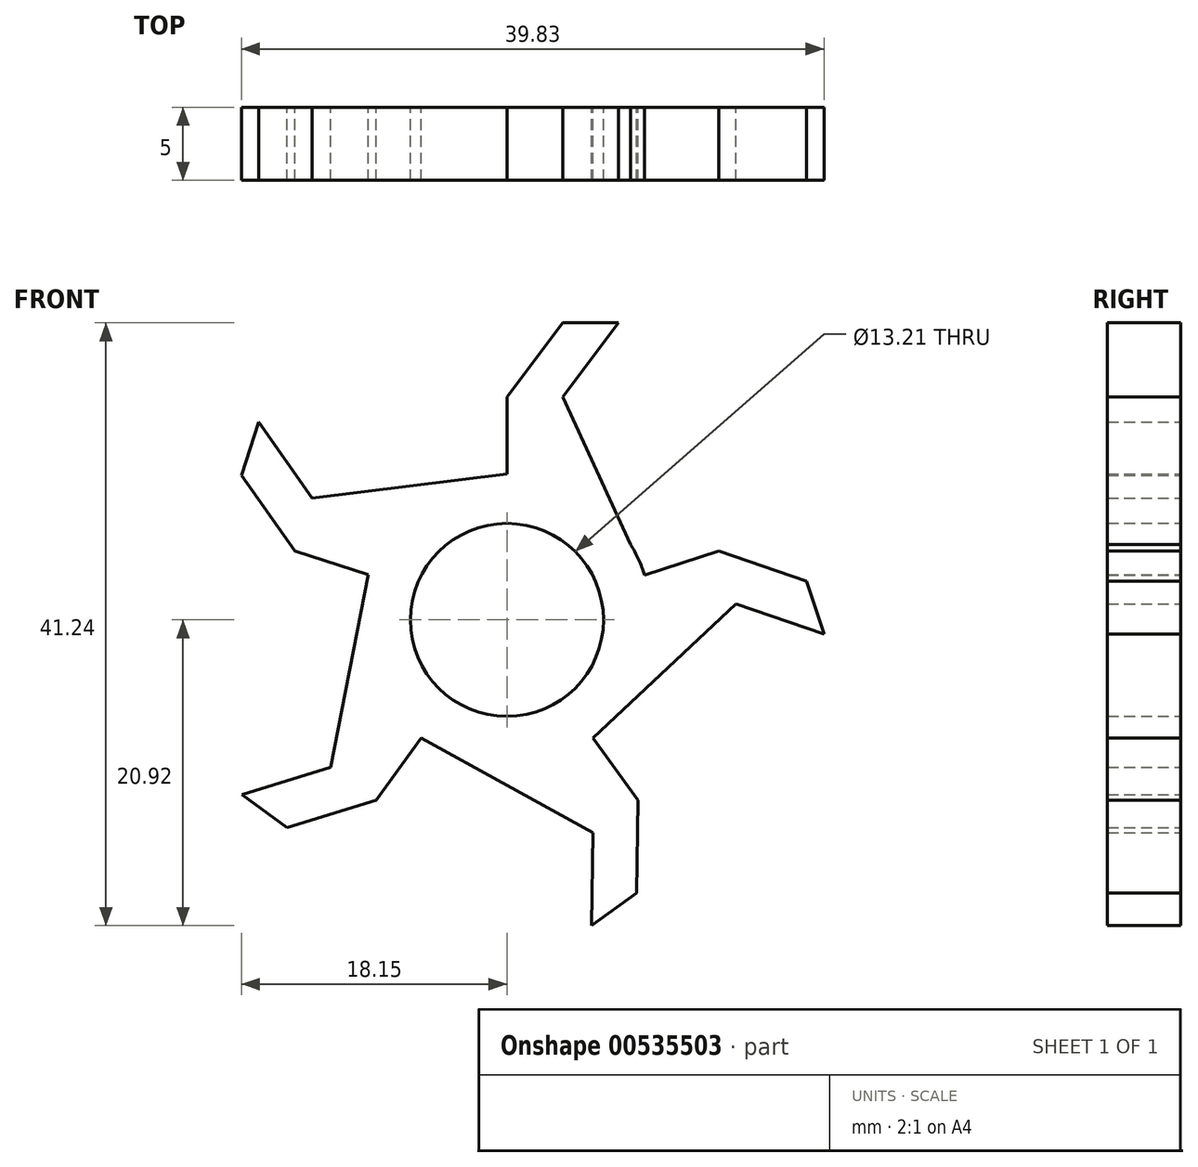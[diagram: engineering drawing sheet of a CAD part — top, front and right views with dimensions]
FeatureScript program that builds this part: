
annotation { "Feature Type Name" : "Feature", "Feature Type Description" : "" }
export const myFeature = defineFeature(function(context is Context, id is Id, definition is map)
    precondition{}
    {
        {
            var Q0;
            Q0=qCreatedBy(makeId("Front.planeOp"),FACE);
            var sketch = newSketch(context, id + "F0", { "sketchPlane" : qUnion([Q0])});
            skCircle(sketch, "E0", {"center": v(0, 0) * mm, "radius": 6.6 * mm});
            skCircle(sketch, "E1", {"center": v(0, 0) * mm, "radius": 9.9 * mm});
            skLineSegment(sketch, "E2", {"start": v(0, 0) * mm, "end": v(0, 15.24) * mm});
            skLineSegment(sketch, "E3", {"start": v(0, 0) * mm, "end": v(3.81, 0) * mm});
            skLineSegment(sketch, "E4", {"start": v(3.81, 0) * mm, "end": v(3.81, 15.24) * mm});
            skLineSegment(sketch, "E5", {"start": v(3.81, 15.24) * mm, "end": v(0, 15.24) * mm});
            skLineSegment(sketch, "E6", {"start": v(3.8, 15.24) * mm, "end": v(7.62, 20.32) * mm});
            skLineSegment(sketch, "E7", {"start": v(7.62, 20.32) * mm, "end": v(3.81, 20.32) * mm});
            skLineSegment(sketch, "E8", {"start": v(3.8, 20.32) * mm, "end": v(0, 15.24) * mm});
            skLineSegment(sketch, "E9", {"start": v(3.81, 15.24) * mm, "end": v(3.81, 20.32) * mm});
            skLineSegment(sketch, "E10.1.0", {"start": v(-16.97, 13.53) * mm, "end": v(-18.15, 9.9) * mm});
            skLineSegment(sketch, "E10.1.1", {"start": v(-18.15, 9.9) * mm, "end": v(-14.5, 4.7) * mm});
            skLineSegment(sketch, "E10.1.2", {"start": v(-13.32, 8.33) * mm, "end": v(-16.97, 13.53) * mm});
            skLineSegment(sketch, "E10.1.3", {"start": v(-13.32, 8.33) * mm, "end": v(-14.5, 4.7) * mm});
            skLineSegment(sketch, "E10.1.4", {"start": v(0, 0) * mm, "end": v(-14.5, 4.7) * mm});
            skLineSegment(sketch, "E10.1.5", {"start": v(1.18, 3.62) * mm, "end": v(-13.32, 8.33) * mm});
            skLineSegment(sketch, "E10.1.6", {"start": v(0, 0) * mm, "end": v(1.18, 3.62) * mm});
            skLineSegment(sketch, "E10.2.0", {"start": v(-18.1, -11.96) * mm, "end": v(-15.03, -14.2) * mm});
            skLineSegment(sketch, "E10.2.1", {"start": v(-15.03, -14.2) * mm, "end": v(-8.96, -12.33) * mm});
            skLineSegment(sketch, "E10.2.2", {"start": v(-12.04, -10.09) * mm, "end": v(-18.1, -11.96) * mm});
            skLineSegment(sketch, "E10.2.3", {"start": v(-12.04, -10.09) * mm, "end": v(-8.96, -12.33) * mm});
            skLineSegment(sketch, "E10.2.4", {"start": v(0, 0) * mm, "end": v(-8.96, -12.33) * mm});
            skLineSegment(sketch, "E10.2.5", {"start": v(-3.08, 2.24) * mm, "end": v(-12.04, -10.09) * mm});
            skLineSegment(sketch, "E10.2.6", {"start": v(0, 0) * mm, "end": v(-3.08, 2.24) * mm});
            skLineSegment(sketch, "E10.3.0", {"start": v(5.78, -20.92) * mm, "end": v(8.86, -18.68) * mm});
            skLineSegment(sketch, "E10.3.1", {"start": v(8.86, -18.68) * mm, "end": v(8.96, -12.33) * mm});
            skLineSegment(sketch, "E10.3.2", {"start": v(5.88, -14.57) * mm, "end": v(5.78, -20.92) * mm});
            skLineSegment(sketch, "E10.3.3", {"start": v(5.88, -14.57) * mm, "end": v(8.96, -12.33) * mm});
            skLineSegment(sketch, "E10.3.4", {"start": v(0, 0) * mm, "end": v(8.96, -12.33) * mm});
            skLineSegment(sketch, "E10.3.5", {"start": v(-3.08, -2.24) * mm, "end": v(5.88, -14.57) * mm});
            skLineSegment(sketch, "E10.3.6", {"start": v(0, 0) * mm, "end": v(-3.08, -2.24) * mm});
            skLineSegment(sketch, "E10.4.0", {"start": v(21.68, -0.97) * mm, "end": v(20.5, 2.66) * mm});
            skLineSegment(sketch, "E10.4.1", {"start": v(20.5, 2.66) * mm, "end": v(14.5, 4.7) * mm});
            skLineSegment(sketch, "E10.4.2", {"start": v(15.67, 1.09) * mm, "end": v(21.68, -0.97) * mm});
            skLineSegment(sketch, "E10.4.3", {"start": v(15.67, 1.09) * mm, "end": v(14.5, 4.7) * mm});
            skLineSegment(sketch, "E10.4.4", {"start": v(0, 0) * mm, "end": v(14.5, 4.7) * mm});
            skLineSegment(sketch, "E10.4.5", {"start": v(1.18, -3.62) * mm, "end": v(15.67, 1.09) * mm});
            skLineSegment(sketch, "E10.4.6", {"start": v(0, 0) * mm, "end": v(1.18, -3.62) * mm});
            skLineSegment(sketch, "E11", {"start": v(-13.32, 8.33) * mm, "end": v(0, 9.98) * mm});
            skLineSegment(sketch, "E12", {"start": v(-12.04, -10.09) * mm, "end": v(-9.5, 3.08) * mm});
            skLineSegment(sketch, "E13", {"start": v(5.88, -14.57) * mm, "end": v(-5.87, -8.08) * mm});
            skLineSegment(sketch, "E14", {"start": v(15.67, 1.09) * mm, "end": v(5.87, -8.08) * mm});
            skLineSegment(sketch, "E15", {"start": v(3.8, 15.24) * mm, "end": v(9.42, 3.06) * mm});
            skSolve(sketch);
        }
        {
            var Q0;
            Q0 = qSketchRegion(id + "F0", true);
            var Q1;
            {var subQ0=sQuery(id+"F0.wireOp",EDGE,"E10.2.5");var subQ1=sQuery(id+"F0.wireOp",EDGE,"E0");var subQ2=makeQuery(id+"F0.imprint","INTERSECT",VERTEX,{"derivedFrom":[subQ1,subQ0]});Q1=makeQuery(id+"F0.imprint","IMPRINT",FACE,{"disambiguationData":[TD([[makeQuery(id+"F0.imprint","IMPRINT",EDGE,{"disambiguationData":[TD([[subQ2,-1.0]])],"derivedFrom":subQ1}),-1.0]])]});}
            var Q2;
            {var subQ0=sQuery(id+"F0.wireOp",EDGE,"E10.3.5");var subQ1=sQuery(id+"F0.wireOp",EDGE,"E0");var subQ2=makeQuery(id+"F0.imprint","INTERSECT",VERTEX,{"derivedFrom":[subQ1,subQ0]});Q2=makeQuery(id+"F0.imprint","IMPRINT",FACE,{"disambiguationData":[TD([[makeQuery(id+"F0.imprint","IMPRINT",EDGE,{"disambiguationData":[TD([[subQ2,-1.0]])],"derivedFrom":subQ1}),-1.0]])]});}
            var Q3;
            {var subQ0=sQuery(id+"F0.wireOp",EDGE,"E10.1.5");var subQ1=sQuery(id+"F0.wireOp",EDGE,"E0");var subQ2=makeQuery(id+"F0.imprint","INTERSECT",VERTEX,{"derivedFrom":[subQ1,subQ0]});Q3=makeQuery(id+"F0.imprint","IMPRINT",FACE,{"disambiguationData":[TD([[makeQuery(id+"F0.imprint","IMPRINT",EDGE,{"disambiguationData":[TD([[subQ2,-1.0]])],"derivedFrom":subQ1}),-1.0]])]});}
            var Q4;
            {var subQ0=sQuery(id+"F0.wireOp",EDGE,"E4");var subQ1=sQuery(id+"F0.wireOp",EDGE,"E0");var subQ2=makeQuery(id+"F0.imprint","INTERSECT",VERTEX,{"derivedFrom":[subQ1,subQ0]});Q4=makeQuery(id+"F0.imprint","IMPRINT",FACE,{"disambiguationData":[TD([[makeQuery(id+"F0.imprint","IMPRINT",EDGE,{"disambiguationData":[TD([[subQ2,-1.0]])],"derivedFrom":subQ1}),-1.0]])]});}
            extrude(context, id + "F1", {"entities" : qUnion([Q0, Q1, Q2, Q3, Q4]), "depth" : 5 * mm, "offsetDistance" : 25.4 * mm});
        }
    });
